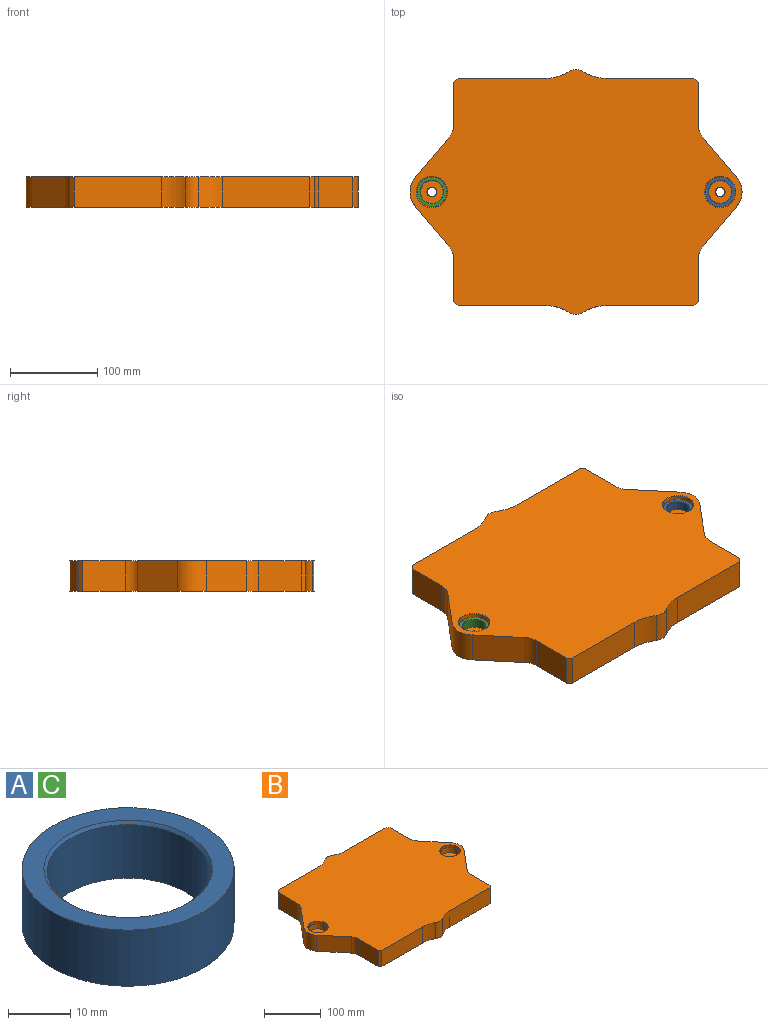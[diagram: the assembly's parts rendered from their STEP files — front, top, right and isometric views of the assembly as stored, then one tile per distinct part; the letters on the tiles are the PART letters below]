
ASSEMBLY  parts=3 mates=2
PART A: 5 faces, bbox 34x34x11 mm
  f0: cylinder r=13mm len=26mm, axis (0,0,-1), area 857.7mm2, adj f3,f4
  f1: cylinder r=17mm len=34mm, axis (0,0,-1), area 1175mm2, adj f2,f3
  f2: plane 34x34mm, normal (0,0,1), area 335.4mm2, adj f1,f4
  f3: plane 34x34mm, normal (0,0,-1), area 377mm2, adj f0,f1
  f4: cone r=13mm half-angle=45deg, axis (0,0,1), area 58.9mm2, adj f0,f2
PART B: 46 faces, bbox 380x280x35 mm
  f0: cylinder r=17mm len=34mm, axis (0,0,1), area 1175mm2, adj f34,f38
  f1: cylinder r=17mm len=34mm, axis (0,0,1), area 1175mm2, adj f35,f36
  f2: cylinder r=5.15mm len=18mm, axis (0,0,1), area 582.5mm2, adj f40,f42
  f3: cylinder r=5.15mm len=18mm, axis (0,0,1), area 582.5mm2, adj f41,f44
  f4: plane 48.67x35mm, normal (1,0,0), area 1703.4mm2, adj f12,f13,f29,f32
  f5: plane 48.67x35mm, normal (-1,0,0), area 1703.4mm2, adj f12,f13,f24,f33
  f6: plane 100.36x35mm, normal (0,-1,0), area 3512.6mm2, adj f12,f13,f17,f30
  f7: plane 100.36x35mm, normal (0,1,0), area 3512.6mm2, adj f12,f13,f15,f32
  f8: plane 48.67x35mm, normal (-1,0,0), area 1703.4mm2, adj f12,f13,f23,f30
  f9: plane 100.36x35mm, normal (0,-1,0), area 3512.6mm2, adj f12,f13,f19,f31
  f10: plane 48.67x35mm, normal (1,0,0), area 1703.4mm2, adj f12,f13,f28,f31
  f11: plane 100.36x35mm, normal (0,1,0), area 3512.6mm2, adj f12,f13,f14,f33
  f12: plane 380x280mm, normal (0,0,1), area 79042.2mm2, adj f4,f5,f6,f7,f8,f9,f10,f11
  f13: plane 380x280mm, normal (0,0,-1), area 80877.3mm2, adj f4,f5,f6,f7,f8,f9,f10,f11
  f14: cylinder r=50mm len=35mm, axis (0,0,1), area 983.6mm2, adj f11,f12,f13,f16
  f15: cylinder r=50mm len=35mm, axis (0,0,1), area 983.6mm2, adj f7,f12,f13,f16
  f16: cylinder r=15mm len=35mm, axis (0,0,1), area 590.2mm2, adj f12,f13,f14,f15
  f17: cylinder r=50mm len=35mm, axis (0,0,1), area 983.6mm2, adj f6,f12,f13,f18
  f18: cylinder r=15mm len=35mm, axis (0,0,1), area 590.2mm2, adj f12,f13,f17,f19
  f19: cylinder r=50mm len=35mm, axis (0,0,1), area 983.6mm2, adj f9,f12,f13,f18
  f20: plane 46.76x39.24mm, normal (-0.77,0.64,0), area 2136.5mm2, adj f12,f13,f21,f24
  f21: cylinder r=25mm len=35mm, axis (0,0,1), area 1221.7mm2, adj f12,f13,f20,f22
  f22: plane 46.76x39.24mm, normal (-0.77,-0.64,0), area 2136.5mm2, adj f12,f13,f21,f23
  f23: cylinder r=21mm len=35mm, axis (0,0,-1), area 513.1mm2, adj f8,f12,f13,f22
  f24: cylinder r=21mm len=35mm, axis (0,0,1), area 513.1mm2, adj f5,f12,f13,f20
  f25: plane 46.76x39.24mm, normal (0.77,0.64,0), area 2136.5mm2, adj f12,f13,f27,f29
  f26: plane 46.76x39.24mm, normal (0.77,-0.64,0), area 2136.5mm2, adj f12,f13,f27,f28
  f27: cylinder r=25mm len=35mm, axis (0,0,1), area 1221.7mm2, adj f12,f13,f25,f26
  f28: cylinder r=21mm len=35mm, axis (0,0,-1), area 513.1mm2, adj f10,f12,f13,f26
  f29: cylinder r=21mm len=35mm, axis (0,0,1), area 513.1mm2, adj f4,f12,f13,f25
  f30: plane 35x5mm, normal (-0.71,-0.71,0), area 247.5mm2, adj f6,f8,f12,f13
  f31: plane 35x5mm, normal (0.71,-0.71,0), area 247.5mm2, adj f9,f10,f12,f13
  f32: plane 35x5mm, normal (0.71,0.71,0), area 247.5mm2, adj f4,f7,f12,f13
  f33: plane 35x5mm, normal (-0.71,0.71,0), area 247.5mm2, adj f5,f11,f12,f13
  f34: plane 34x34mm, normal (0,0,1), area 807.6mm2, adj f0,f44
  f35: plane 34x34mm, normal (0,0,1), area 807.6mm2, adj f1,f42
  f36: plane 35x35mm, normal (0,0,1), area 54.2mm2, adj f1,f37
  f37: cylinder r=17.5mm len=35mm, axis (0,0,1), area 494.8mm2, adj f36,f43
  f38: plane 35x35mm, normal (0,0,1), area 54.2mm2, adj f0,f39
  f39: cylinder r=17.5mm len=35mm, axis (0,0,1), area 494.8mm2, adj f38,f45
  f40: cone r=5.15mm half-angle=45deg, axis (0,0,-1), area 24mm2, adj f2,f13
  f41: cone r=5.15mm half-angle=45deg, axis (0,0,-1), area 24mm2, adj f3,f13
  f42: cone r=5.15mm half-angle=45deg, axis (0,0,1), area 24mm2, adj f2,f35
  f43: cone r=17.5mm half-angle=45deg, axis (0,0,1), area 78.9mm2, adj f12,f37
  f44: cone r=5.15mm half-angle=45deg, axis (0,0,1), area 24mm2, adj f3,f34
  f45: cone r=17.5mm half-angle=45deg, axis (0,0,1), area 78.9mm2, adj f12,f39
PART C: same geometry as A
PLACE A t=(165,0,19)mm
PLACE B at identity
PLACE C t=(-165,0,19)mm
MATE fastened A.f1 <-> B.f1  axis (0,0,-1) through (165,0,19)mm
MATE fastened C.f0 <-> B.f0  axis (0,0,-1) through (-165,0,19)mm
